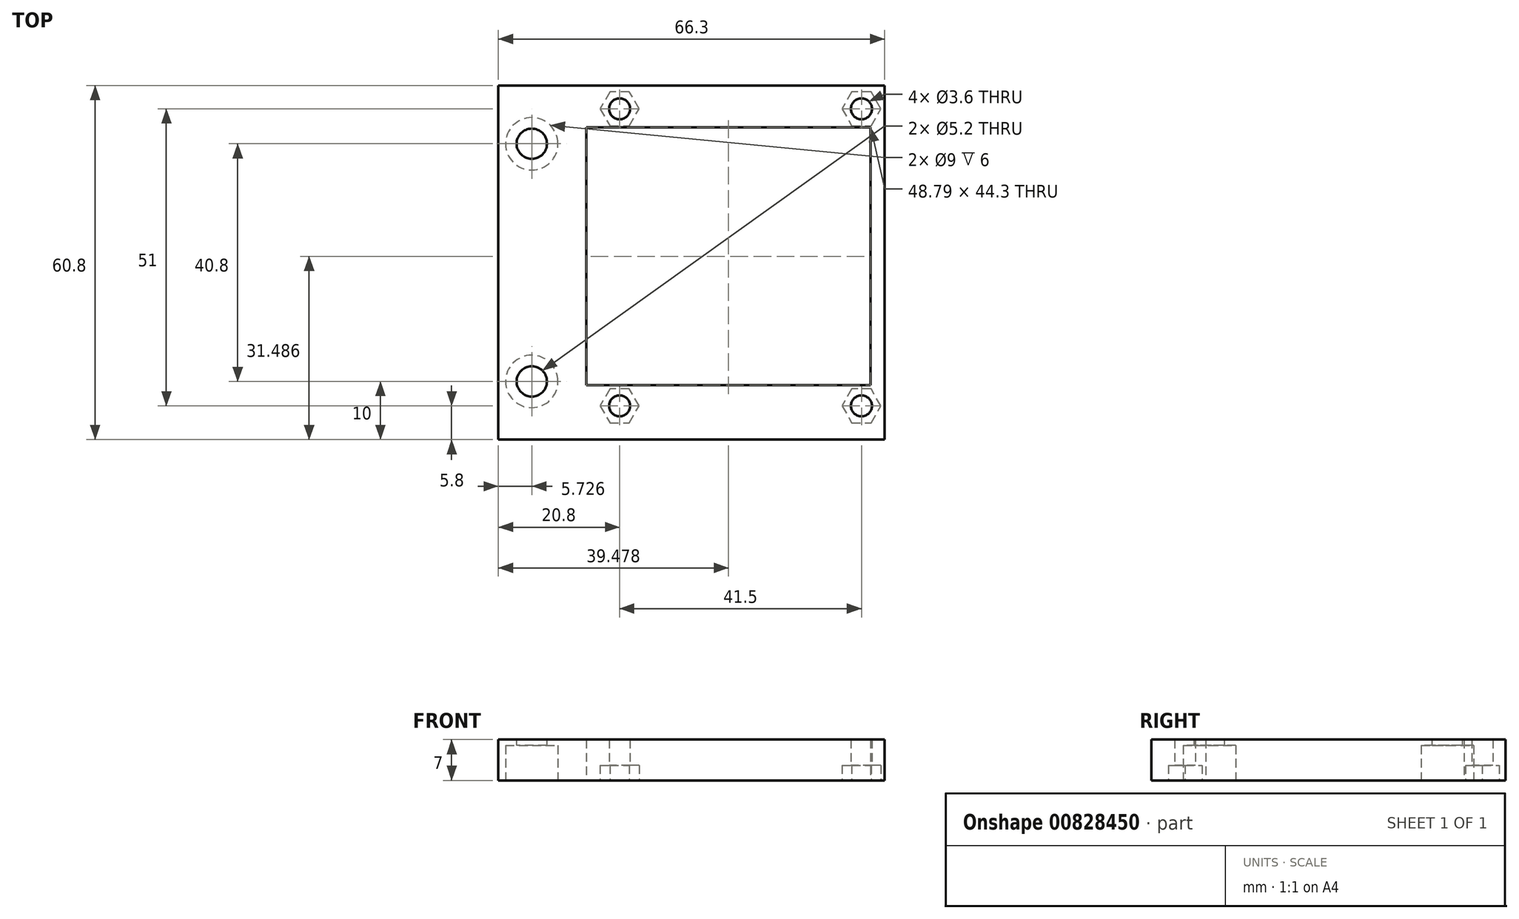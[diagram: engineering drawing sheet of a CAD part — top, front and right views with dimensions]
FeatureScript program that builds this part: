
annotation { "Feature Type Name" : "Feature", "Feature Type Description" : "" }
export const myFeature = defineFeature(function(context is Context, id is Id, definition is map)
    precondition{}
    {
        {
            assignVariable(context, id + "F0", {"name" : "m5_countersink_depth", "anyValue" : 6});
        }
        {
            assignVariable(context, id + "F1", {"name" : "m3_nut_countersink_depth", "anyValue" : 2.6});
        }
        {
            var Q0;
            Q0=qCreatedBy(makeId("Top.planeOp"),FACE);
            var sketch = newSketch(context, id + "F2", { "sketchPlane" : qUnion([Q0])});
            skLineSegment(sketch, "E0.bottom", {"start": v(0, 0) * mm, "end": v(51.3, 0) * mm});
            skLineSegment(sketch, "E0.top", {"start": v(0, -60.8) * mm, "end": v(51.3, -60.8) * mm});
            skLineSegment(sketch, "E0.left", {"start": v(0, 0) * mm, "end": v(0, -60.8) * mm});
            skLineSegment(sketch, "E0.right", {"start": v(51.3, 0) * mm, "end": v(51.3, -60.8) * mm});
            skCircle(sketch, "E1", {"center": v(5.8, -4) * mm, "radius": 1.8 * mm});
            skCircle(sketch, "E2", {"center": v(5.8, -55) * mm, "radius": 1.8 * mm});
            skCircle(sketch, "E3", {"center": v(47.3, -55) * mm, "radius": 1.8 * mm});
            skCircle(sketch, "E4", {"center": v(47.3, -4) * mm, "radius": 1.8 * mm});
            skLineSegment(sketch, "E5", {"start": v(5.8, -56.8) * mm, "end": v(5.8, -60.8) * mm, "construction": true});
            skLineSegment(sketch, "E6", {"start": v(4, -55) * mm, "end": v(0, -55) * mm, "construction": true});
            skLineSegment(sketch, "E7", {"start": v(47.3, -4) * mm, "end": v(51.3, -4) * mm, "construction": true});
            skLineSegment(sketch, "E8", {"start": v(47.3, -4) * mm, "end": v(47.3, 0) * mm, "construction": true});
            skLineSegment(sketch, "E9.bottom", {"start": v(0.08, -7.16) * mm, "end": v(48.87, -7.16) * mm});
            skLineSegment(sketch, "E9.top", {"start": v(0.08, -51.46) * mm, "end": v(48.87, -51.46) * mm});
            skLineSegment(sketch, "E9.left", {"start": v(0.08, -7.16) * mm, "end": v(0.08, -51.46) * mm});
            skLineSegment(sketch, "E9.right", {"start": v(48.87, -7.16) * mm, "end": v(48.87, -51.46) * mm});
            skSolve(sketch);
        }
        {
            var Q0;
            Q0=makeQuery(id+"F2.imprint","IMPRINT",FACE,{"disambiguationData":[TD([[makeQuery(id+"F2.imprint","IMPRINT",EDGE,{"derivedFrom":sQuery(id+"F2.wireOp",EDGE,"E0.bottom")}),-1.0]])]});
            extrude(context, id + "F3", {"entities" : qUnion([Q0]), "depth" : 7 * mm, "offsetDistance" : 25 * mm});
        }
        {
            var Q0;
            Q0=makeQuery(id+"F3.opExtrude","SWEPT_FACE",FACE,{"disambiguationData":[OSD([sQuery(id+"F2.wireOp",EDGE,"E0.left")])]});
            extrude(context, id + "F4", {"entities" : qUnion([Q0]), "operationType" : NewBodyOperationType.ADD, "depth" : 15 * mm, "offsetDistance" : 25 * mm});
        }
        {
            var Q0;
            {var subQ0=sQuery(id+"F2.wireOp",EDGE,"E0.left");Q0=makeQuery(id+"F4.boolean.opBoolean","MERGE",FACE,{"derivedFrom":[makeQuery(id+"F3.opExtrude","CAP_FACE",FACE,{"disambiguationData":[OSD([sQuery(id+"F2.wireOp",EDGE,"E0.bottom"),sQuery(id+"F2.wireOp",EDGE,"E0.top"),subQ0,sQuery(id+"F2.wireOp",EDGE,"E0.right"),sQuery(id+"F2.wireOp",EDGE,"R8pAmf2F-biWS-PgLo-OTuY-xoEfuvJFqgsZ.bottom"),sQuery(id+"F2.wireOp",EDGE,"R8pAmf2F-biWS-PgLo-OTuY-xoEfuvJFqgsZ.top"),sQuery(id+"F2.wireOp",EDGE,"R8pAmf2F-biWS-PgLo-OTuY-xoEfuvJFqgsZ.left"),sQuery(id+"F2.wireOp",EDGE,"R8pAmf2F-biWS-PgLo-OTuY-xoEfuvJFqgsZ.right"),sQuery(id+"F2.wireOp",EDGE,"E1"),sQuery(id+"F2.wireOp",EDGE,"E2"),sQuery(id+"F2.wireOp",EDGE,"E3"),sQuery(id+"F2.wireOp",EDGE,"E4")])],"isStart":false}),makeQuery(id+"F4.opExtrude","SWEPT_FACE",FACE,{"disambiguationData":[OSD([subQ0]),TDD([makeQuery(id+"F3.opExtrude","CAP_EDGE",EDGE,{"disambiguationData":[OSD([subQ0])],"isStart":false})])]})]});}
            var sketch = newSketch(context, id + "F5", { "sketchPlane" : qUnion([Q0])});
            skCircle(sketch, "E10", {"center": v(-9.27, -10) * mm, "radius": 2.6 * mm});
            skCircle(sketch, "E11", {"center": v(-9.27, -50.8) * mm, "radius": 2.6 * mm});
            skLineSegment(sketch, "E12", {"start": v(-9.27, -10) * mm, "end": v(-9.27, -50.8) * mm, "construction": true});
            skLineSegment(sketch, "E13", {"start": v(-9.27, -10) * mm, "end": v(-9.27, 0) * mm, "construction": true});
            skLineSegment(sketch, "E14", {"start": v(-9.27, -50.8) * mm, "end": v(-9.27, -60.8) * mm, "construction": true});
            skSolve(sketch);
        }
        {
            var Q0;
            Q0=makeQuery(id+"F5.imprint","IMPRINT",FACE,{"disambiguationData":[TD([[makeQuery(id+"F5.imprint","IMPRINT",EDGE,{"derivedFrom":sQuery(id+"F5.wireOp",EDGE,"E10")}),1.0]])]});
            var Q1;
            Q1=makeQuery(id+"F5.imprint","IMPRINT",FACE,{"disambiguationData":[TD([[makeQuery(id+"F5.imprint","IMPRINT",EDGE,{"derivedFrom":sQuery(id+"F5.wireOp",EDGE,"E11")}),1.0]])]});
            extrude(context, id + "F6", {"entities" : qUnion([Q0, Q1]), "operationType" : NewBodyOperationType.REMOVE, "oppositeDirection" : true, "depth" : 25 * mm, "offsetDistance" : 25 * mm});
        }
        {
            var Q0;
            {var subQ0=sQuery(id+"F2.wireOp",EDGE,"E0.left");Q0=makeQuery(id+"F4.boolean.opBoolean","MERGE",FACE,{"derivedFrom":[makeQuery(id+"F3.opExtrude","CAP_FACE",FACE,{"disambiguationData":[OSD([sQuery(id+"F2.wireOp",EDGE,"E0.bottom"),sQuery(id+"F2.wireOp",EDGE,"E0.top"),subQ0,sQuery(id+"F2.wireOp",EDGE,"E0.right"),sQuery(id+"F2.wireOp",EDGE,"R8pAmf2F-biWS-PgLo-OTuY-xoEfuvJFqgsZ.bottom"),sQuery(id+"F2.wireOp",EDGE,"R8pAmf2F-biWS-PgLo-OTuY-xoEfuvJFqgsZ.top"),sQuery(id+"F2.wireOp",EDGE,"R8pAmf2F-biWS-PgLo-OTuY-xoEfuvJFqgsZ.left"),sQuery(id+"F2.wireOp",EDGE,"R8pAmf2F-biWS-PgLo-OTuY-xoEfuvJFqgsZ.right"),sQuery(id+"F2.wireOp",EDGE,"E1"),sQuery(id+"F2.wireOp",EDGE,"E2"),sQuery(id+"F2.wireOp",EDGE,"E3"),sQuery(id+"F2.wireOp",EDGE,"E4")])],"isStart":true}),makeQuery(id+"F4.opExtrude","SWEPT_FACE",FACE,{"disambiguationData":[OSD([subQ0]),TDD([makeQuery(id+"F3.opExtrude","CAP_EDGE",EDGE,{"disambiguationData":[OSD([subQ0])],"isStart":true})])]})]});}
            var sketch = newSketch(context, id + "F7", { "sketchPlane" : qUnion([Q0])});
            skCircle(sketch, "E15.cCircle", {"center": v(5.8, 55) * mm, "radius": 2.9 * mm, "construction": true});
            skLineSegment(sketch, "E15.0", {"start": v(9.15, 55) * mm, "end": v(7.47, 52.1) * mm});
            skLineSegment(sketch, "E15.1", {"start": v(7.47, 52.1) * mm, "end": v(4.13, 52.1) * mm});
            skLineSegment(sketch, "E15.2", {"start": v(4.13, 52.1) * mm, "end": v(2.45, 55) * mm});
            skLineSegment(sketch, "E15.3", {"start": v(2.45, 55) * mm, "end": v(4.13, 57.9) * mm});
            skLineSegment(sketch, "E15.4", {"start": v(4.13, 57.9) * mm, "end": v(7.47, 57.9) * mm});
            skLineSegment(sketch, "E15.5", {"start": v(7.47, 57.9) * mm, "end": v(9.15, 55) * mm});
            skPoint(sketch, "E15.0.midPoint", {"position": v(8.31, 53.55) * mm});
            skCircle(sketch, "E16.cCircle", {"center": v(47.3, 55) * mm, "radius": 2.9 * mm, "construction": true});
            skLineSegment(sketch, "E16.0", {"start": v(50.65, 55) * mm, "end": v(48.97, 52.1) * mm});
            skLineSegment(sketch, "E16.1", {"start": v(48.97, 52.1) * mm, "end": v(45.63, 52.1) * mm});
            skLineSegment(sketch, "E16.2", {"start": v(45.63, 52.1) * mm, "end": v(43.95, 55) * mm});
            skLineSegment(sketch, "E16.3", {"start": v(43.95, 55) * mm, "end": v(45.63, 57.9) * mm});
            skLineSegment(sketch, "E16.4", {"start": v(45.63, 57.9) * mm, "end": v(48.97, 57.9) * mm});
            skLineSegment(sketch, "E16.5", {"start": v(48.97, 57.9) * mm, "end": v(50.65, 55) * mm});
            skPoint(sketch, "E16.0.midPoint", {"position": v(49.81, 53.55) * mm});
            skCircle(sketch, "E17.cCircle", {"center": v(5.8, 4) * mm, "radius": 2.9 * mm, "construction": true});
            skLineSegment(sketch, "E17.0", {"start": v(9.15, 4) * mm, "end": v(7.47, 1.1) * mm});
            skLineSegment(sketch, "E17.1", {"start": v(7.47, 1.1) * mm, "end": v(4.13, 1.1) * mm});
            skLineSegment(sketch, "E17.2", {"start": v(4.13, 1.1) * mm, "end": v(2.45, 4) * mm});
            skLineSegment(sketch, "E17.3", {"start": v(2.45, 4) * mm, "end": v(4.13, 6.9) * mm});
            skLineSegment(sketch, "E17.4", {"start": v(4.13, 6.9) * mm, "end": v(7.47, 6.9) * mm});
            skLineSegment(sketch, "E17.5", {"start": v(7.47, 6.9) * mm, "end": v(9.15, 4) * mm});
            skPoint(sketch, "E17.0.midPoint", {"position": v(8.31, 2.55) * mm});
            skCircle(sketch, "E18.cCircle", {"center": v(47.3, 4) * mm, "radius": 2.9 * mm, "construction": true});
            skLineSegment(sketch, "E18.0", {"start": v(50.65, 4) * mm, "end": v(48.97, 1.1) * mm});
            skLineSegment(sketch, "E18.1", {"start": v(48.97, 1.1) * mm, "end": v(45.63, 1.1) * mm});
            skLineSegment(sketch, "E18.2", {"start": v(45.63, 1.1) * mm, "end": v(43.95, 4) * mm});
            skLineSegment(sketch, "E18.3", {"start": v(43.95, 4) * mm, "end": v(45.63, 6.9) * mm});
            skLineSegment(sketch, "E18.4", {"start": v(45.63, 6.9) * mm, "end": v(48.97, 6.9) * mm});
            skLineSegment(sketch, "E18.5", {"start": v(48.97, 6.9) * mm, "end": v(50.65, 4) * mm});
            skPoint(sketch, "E18.0.midPoint", {"position": v(49.81, 2.55) * mm});
            skSolve(sketch);
        }
        {
            var Q0;
            Q0=makeQuery(id+"F7.imprint","IMPRINT",FACE,{"disambiguationData":[TD([[makeQuery(id+"F7.imprint","IMPRINT",EDGE,{"derivedFrom":sQuery(id+"F7.wireOp",EDGE,"E15.0")}),-1.0]])]});
            var Q1;
            Q1=makeQuery(id+"F7.imprint","IMPRINT",FACE,{"disambiguationData":[TD([[makeQuery(id+"F7.imprint","IMPRINT",EDGE,{"derivedFrom":sQuery(id+"F7.wireOp",EDGE,"E16.0")}),-1.0]])]});
            var Q2;
            Q2=makeQuery(id+"F7.imprint","IMPRINT",FACE,{"disambiguationData":[TD([[makeQuery(id+"F7.imprint","IMPRINT",EDGE,{"derivedFrom":sQuery(id+"F7.wireOp",EDGE,"E18.0")}),-1.0]])]});
            var Q3;
            Q3=makeQuery(id+"F7.imprint","IMPRINT",FACE,{"disambiguationData":[TD([[makeQuery(id+"F7.imprint","IMPRINT",EDGE,{"derivedFrom":sQuery(id+"F7.wireOp",EDGE,"E17.0")}),-1.0]])]});
            extrude(context, id + "F8", {"entities" : qUnion([Q0, Q1, Q2, Q3]), "operationType" : NewBodyOperationType.REMOVE, "oppositeDirection" : true, "depth" : (getVariable(context, 'm3_nut_countersink_depth')) * mm, "offsetDistance" : 25 * mm});
        }
        {
            var Q0;
            {var subQ0=sQuery(id+"F2.wireOp",EDGE,"E0.left");Q0=makeQuery(id+"F4.boolean.opBoolean","MERGE",FACE,{"derivedFrom":[makeQuery(id+"F3.opExtrude","CAP_FACE",FACE,{"disambiguationData":[OSD([sQuery(id+"F2.wireOp",EDGE,"E0.bottom"),sQuery(id+"F2.wireOp",EDGE,"E0.top"),subQ0,sQuery(id+"F2.wireOp",EDGE,"E0.right"),sQuery(id+"F2.wireOp",EDGE,"R8pAmf2F-biWS-PgLo-OTuY-xoEfuvJFqgsZ.bottom"),sQuery(id+"F2.wireOp",EDGE,"R8pAmf2F-biWS-PgLo-OTuY-xoEfuvJFqgsZ.top"),sQuery(id+"F2.wireOp",EDGE,"R8pAmf2F-biWS-PgLo-OTuY-xoEfuvJFqgsZ.left"),sQuery(id+"F2.wireOp",EDGE,"R8pAmf2F-biWS-PgLo-OTuY-xoEfuvJFqgsZ.right"),sQuery(id+"F2.wireOp",EDGE,"E1"),sQuery(id+"F2.wireOp",EDGE,"E2"),sQuery(id+"F2.wireOp",EDGE,"E3"),sQuery(id+"F2.wireOp",EDGE,"E4")])],"isStart":true}),makeQuery(id+"F4.opExtrude","SWEPT_FACE",FACE,{"disambiguationData":[OSD([subQ0]),TDD([makeQuery(id+"F3.opExtrude","CAP_EDGE",EDGE,{"disambiguationData":[OSD([subQ0])],"isStart":true})])]})]});}
            var sketch = newSketch(context, id + "F9", { "sketchPlane" : qUnion([Q0])});
            skCircle(sketch, "E19", {"center": v(-9.27, 10) * mm, "radius": 4.5 * mm});
            skCircle(sketch, "E20", {"center": v(-9.27, 50.8) * mm, "radius": 4.5 * mm});
            skSolve(sketch);
        }
        {
            var Q0;
            Q0=makeQuery(id+"F9.imprint","IMPRINT",FACE,{"disambiguationData":[TD([[makeQuery(id+"F9.imprint","IMPRINT",EDGE,{"derivedFrom":sQuery(id+"F9.wireOp",EDGE,"E19")}),1.0]])]});
            var Q1;
            Q1=makeQuery(id+"F9.imprint","IMPRINT",FACE,{"disambiguationData":[TD([[makeQuery(id+"F9.imprint","IMPRINT",EDGE,{"derivedFrom":sQuery(id+"F9.wireOp",EDGE,"E20")}),1.0]])]});
            extrude(context, id + "F10", {"entities" : qUnion([Q0, Q1]), "operationType" : NewBodyOperationType.REMOVE, "oppositeDirection" : true, "depth" : (getVariable(context, 'm5_countersink_depth')) * mm, "offsetDistance" : 25 * mm});
        }
    });
